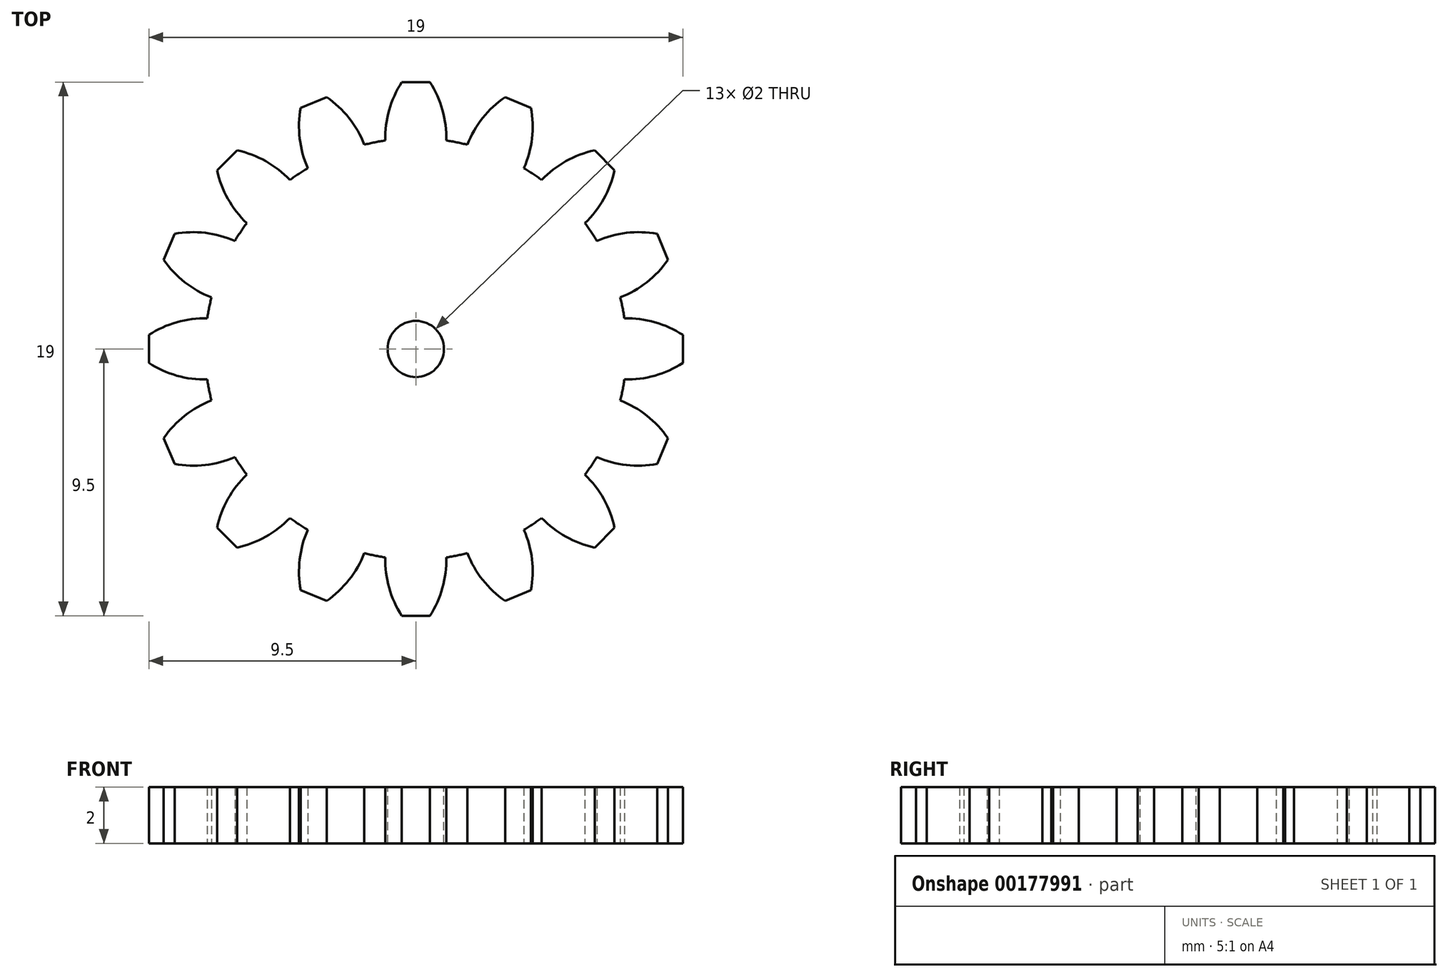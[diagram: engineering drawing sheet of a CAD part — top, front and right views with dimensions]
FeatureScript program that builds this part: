
annotation { "Feature Type Name" : "Feature", "Feature Type Description" : "" }
export const myFeature = defineFeature(function(context is Context, id is Id, definition is map)
    precondition{}
    {
        {
            var Q0;
            Q0=qCreatedBy(makeId("Top.planeOp"),FACE);
            var sketch = newSketch(context, id + "F0", { "sketchPlane" : qUnion([Q0])});
            skCircle(sketch, "E0", {"center": v(0, 0) * mm, "radius": 7.5 * mm});
            skLineSegment(sketch, "E1", {"start": v(0, 0) * mm, "end": v(0, 7.5) * mm, "construction": true});
            skLineSegment(sketch, "E2", {"start": v(0, 7.5) * mm, "end": v(0, 9.5) * mm, "construction": true});
            skLineSegment(sketch, "E3", {"start": v(0, 9.5) * mm, "end": v(-0.5, 9.5) * mm});
            skArc(sketch, "E4", {"start": v(-0.5, 9.5) * mm, "mid": v(-0.95, 8.5) * mm, "end": v(-1.09, 7.42) * mm});
            skLineSegment(sketch, "E5.MirrorCS", {"start": v(0, 9.5) * mm, "end": v(0.5, 9.5) * mm});
            skArc(sketch, "E6.MirrorCS", {"start": v(0.5, 9.5) * mm, "mid": v(0.95, 8.5) * mm, "end": v(1.09, 7.42) * mm});
            skArc(sketch, "E7.1.0", {"start": v(-4.1, 8.59) * mm, "mid": v(-4.13, 7.5) * mm, "end": v(-3.85, 6.44) * mm});
            skLineSegment(sketch, "E7.1.1", {"start": v(-3.64, 8.78) * mm, "end": v(-4.1, 8.59) * mm});
            skLineSegment(sketch, "E7.1.2", {"start": v(-3.64, 8.78) * mm, "end": v(-3.17, 8.97) * mm});
            skArc(sketch, "E7.1.3", {"start": v(-3.17, 8.97) * mm, "mid": v(-2.38, 8.22) * mm, "end": v(-1.83, 7.27) * mm});
            skArc(sketch, "E7.2.0", {"start": v(-7.07, 6.36) * mm, "mid": v(-6.69, 5.34) * mm, "end": v(-6.02, 4.48) * mm});
            skLineSegment(sketch, "E7.2.1", {"start": v(-6.72, 6.72) * mm, "end": v(-7.07, 6.36) * mm});
            skLineSegment(sketch, "E7.2.2", {"start": v(-6.72, 6.72) * mm, "end": v(-6.36, 7.07) * mm});
            skArc(sketch, "E7.2.3", {"start": v(-6.36, 7.07) * mm, "mid": v(-5.34, 6.69) * mm, "end": v(-4.48, 6.02) * mm});
            skArc(sketch, "E7.3.0", {"start": v(-8.97, 3.17) * mm, "mid": v(-8.22, 2.38) * mm, "end": v(-7.27, 1.83) * mm});
            skLineSegment(sketch, "E7.3.1", {"start": v(-8.78, 3.64) * mm, "end": v(-8.97, 3.17) * mm});
            skLineSegment(sketch, "E7.3.2", {"start": v(-8.78, 3.64) * mm, "end": v(-8.59, 4.1) * mm});
            skArc(sketch, "E7.3.3", {"start": v(-8.59, 4.1) * mm, "mid": v(-7.5, 4.13) * mm, "end": v(-6.44, 3.85) * mm});
            skArc(sketch, "E7.4.0", {"start": v(-9.5, -0.5) * mm, "mid": v(-8.5, -0.95) * mm, "end": v(-7.42, -1.09) * mm});
            skLineSegment(sketch, "E7.4.1", {"start": v(-9.5, 0) * mm, "end": v(-9.5, -0.5) * mm});
            skLineSegment(sketch, "E7.4.2", {"start": v(-9.5, 0) * mm, "end": v(-9.5, 0.5) * mm});
            skArc(sketch, "E7.4.3", {"start": v(-9.5, 0.5) * mm, "mid": v(-8.5, 0.95) * mm, "end": v(-7.42, 1.09) * mm});
            skArc(sketch, "E7.5.0", {"start": v(-8.59, -4.1) * mm, "mid": v(-7.5, -4.13) * mm, "end": v(-6.44, -3.85) * mm});
            skLineSegment(sketch, "E7.5.1", {"start": v(-8.78, -3.64) * mm, "end": v(-8.59, -4.1) * mm});
            skLineSegment(sketch, "E7.5.2", {"start": v(-8.78, -3.64) * mm, "end": v(-8.97, -3.17) * mm});
            skArc(sketch, "E7.5.3", {"start": v(-8.97, -3.17) * mm, "mid": v(-8.22, -2.38) * mm, "end": v(-7.27, -1.83) * mm});
            skArc(sketch, "E7.6.0", {"start": v(-6.36, -7.07) * mm, "mid": v(-5.34, -6.69) * mm, "end": v(-4.48, -6.02) * mm});
            skLineSegment(sketch, "E7.6.1", {"start": v(-6.72, -6.72) * mm, "end": v(-6.36, -7.07) * mm});
            skLineSegment(sketch, "E7.6.2", {"start": v(-6.72, -6.72) * mm, "end": v(-7.07, -6.36) * mm});
            skArc(sketch, "E7.6.3", {"start": v(-7.07, -6.36) * mm, "mid": v(-6.69, -5.34) * mm, "end": v(-6.02, -4.48) * mm});
            skArc(sketch, "E7.7.0", {"start": v(-3.17, -8.97) * mm, "mid": v(-2.38, -8.22) * mm, "end": v(-1.83, -7.27) * mm});
            skLineSegment(sketch, "E7.7.1", {"start": v(-3.64, -8.78) * mm, "end": v(-3.17, -8.97) * mm});
            skLineSegment(sketch, "E7.7.2", {"start": v(-3.64, -8.78) * mm, "end": v(-4.1, -8.59) * mm});
            skArc(sketch, "E7.7.3", {"start": v(-4.1, -8.59) * mm, "mid": v(-4.13, -7.5) * mm, "end": v(-3.85, -6.44) * mm});
            skArc(sketch, "E7.8.0", {"start": v(0.5, -9.5) * mm, "mid": v(0.95, -8.5) * mm, "end": v(1.09, -7.42) * mm});
            skLineSegment(sketch, "E7.8.1", {"start": v(0, -9.5) * mm, "end": v(0.5, -9.5) * mm});
            skLineSegment(sketch, "E7.8.2", {"start": v(0, -9.5) * mm, "end": v(-0.5, -9.5) * mm});
            skArc(sketch, "E7.8.3", {"start": v(-0.5, -9.5) * mm, "mid": v(-0.95, -8.5) * mm, "end": v(-1.09, -7.42) * mm});
            skArc(sketch, "E7.9.0", {"start": v(4.1, -8.59) * mm, "mid": v(4.13, -7.5) * mm, "end": v(3.85, -6.44) * mm});
            skLineSegment(sketch, "E7.9.1", {"start": v(3.64, -8.78) * mm, "end": v(4.1, -8.59) * mm});
            skLineSegment(sketch, "E7.9.2", {"start": v(3.64, -8.78) * mm, "end": v(3.17, -8.97) * mm});
            skArc(sketch, "E7.9.3", {"start": v(3.17, -8.97) * mm, "mid": v(2.38, -8.22) * mm, "end": v(1.83, -7.27) * mm});
            skArc(sketch, "E7.10.0", {"start": v(7.07, -6.36) * mm, "mid": v(6.69, -5.34) * mm, "end": v(6.02, -4.48) * mm});
            skLineSegment(sketch, "E7.10.1", {"start": v(6.72, -6.72) * mm, "end": v(7.07, -6.36) * mm});
            skLineSegment(sketch, "E7.10.2", {"start": v(6.72, -6.72) * mm, "end": v(6.36, -7.07) * mm});
            skArc(sketch, "E7.10.3", {"start": v(6.36, -7.07) * mm, "mid": v(5.34, -6.69) * mm, "end": v(4.48, -6.02) * mm});
            skArc(sketch, "E7.11.0", {"start": v(8.97, -3.17) * mm, "mid": v(8.22, -2.38) * mm, "end": v(7.27, -1.83) * mm});
            skLineSegment(sketch, "E7.11.1", {"start": v(8.78, -3.64) * mm, "end": v(8.97, -3.17) * mm});
            skLineSegment(sketch, "E7.11.2", {"start": v(8.78, -3.64) * mm, "end": v(8.59, -4.1) * mm});
            skArc(sketch, "E7.11.3", {"start": v(8.59, -4.1) * mm, "mid": v(7.5, -4.13) * mm, "end": v(6.44, -3.85) * mm});
            skArc(sketch, "E7.12.0", {"start": v(9.5, 0.5) * mm, "mid": v(8.5, 0.95) * mm, "end": v(7.42, 1.09) * mm});
            skLineSegment(sketch, "E7.12.1", {"start": v(9.5, 0) * mm, "end": v(9.5, 0.5) * mm});
            skLineSegment(sketch, "E7.12.2", {"start": v(9.5, 0) * mm, "end": v(9.5, -0.5) * mm});
            skArc(sketch, "E7.12.3", {"start": v(9.5, -0.5) * mm, "mid": v(8.5, -0.95) * mm, "end": v(7.42, -1.09) * mm});
            skArc(sketch, "E7.13.0", {"start": v(8.59, 4.1) * mm, "mid": v(7.5, 4.13) * mm, "end": v(6.44, 3.85) * mm});
            skLineSegment(sketch, "E7.13.1", {"start": v(8.78, 3.64) * mm, "end": v(8.59, 4.1) * mm});
            skLineSegment(sketch, "E7.13.2", {"start": v(8.78, 3.64) * mm, "end": v(8.97, 3.17) * mm});
            skArc(sketch, "E7.13.3", {"start": v(8.97, 3.17) * mm, "mid": v(8.22, 2.38) * mm, "end": v(7.27, 1.83) * mm});
            skArc(sketch, "E7.14.0", {"start": v(6.36, 7.07) * mm, "mid": v(5.34, 6.69) * mm, "end": v(4.48, 6.02) * mm});
            skLineSegment(sketch, "E7.14.1", {"start": v(6.72, 6.72) * mm, "end": v(6.36, 7.07) * mm});
            skLineSegment(sketch, "E7.14.2", {"start": v(6.72, 6.72) * mm, "end": v(7.07, 6.36) * mm});
            skArc(sketch, "E7.14.3", {"start": v(7.07, 6.36) * mm, "mid": v(6.69, 5.34) * mm, "end": v(6.02, 4.48) * mm});
            skArc(sketch, "E7.15.0", {"start": v(3.17, 8.97) * mm, "mid": v(2.38, 8.22) * mm, "end": v(1.83, 7.27) * mm});
            skLineSegment(sketch, "E7.15.1", {"start": v(3.64, 8.78) * mm, "end": v(3.17, 8.97) * mm});
            skLineSegment(sketch, "E7.15.2", {"start": v(3.64, 8.78) * mm, "end": v(4.1, 8.59) * mm});
            skArc(sketch, "E7.15.3", {"start": v(4.1, 8.59) * mm, "mid": v(4.13, 7.5) * mm, "end": v(3.85, 6.44) * mm});
            skSolve(sketch);
        }
        {
            var Q0;
            Q0 = qSketchRegion(id + "F0", true);
            extrude(context, id + "F1", {"entities" : qUnion([Q0]), "depth" : 2 * mm});
        }
        {
            var Q0;
            Q0=makeQuery(id+"F1.opExtrude","CAP_FACE",FACE,{"disambiguationData":[OSD([sQuery(id+"F0.wireOp",EDGE,"E0"),sQuery(id+"F0.wireOp",EDGE,"E3"),sQuery(id+"F0.wireOp",EDGE,"E4"),sQuery(id+"F0.wireOp",EDGE,"E5.MirrorCS"),sQuery(id+"F0.wireOp",EDGE,"E6.MirrorCS"),sQuery(id+"F0.wireOp",EDGE,"E7.1.0"),sQuery(id+"F0.wireOp",EDGE,"E7.1.1"),sQuery(id+"F0.wireOp",EDGE,"E7.1.2"),sQuery(id+"F0.wireOp",EDGE,"E7.1.3"),sQuery(id+"F0.wireOp",EDGE,"E7.2.0"),sQuery(id+"F0.wireOp",EDGE,"E7.2.1"),sQuery(id+"F0.wireOp",EDGE,"E7.2.2"),sQuery(id+"F0.wireOp",EDGE,"E7.2.3"),sQuery(id+"F0.wireOp",EDGE,"E7.3.0"),sQuery(id+"F0.wireOp",EDGE,"E7.3.1"),sQuery(id+"F0.wireOp",EDGE,"E7.3.2"),sQuery(id+"F0.wireOp",EDGE,"E7.3.3"),sQuery(id+"F0.wireOp",EDGE,"E7.4.0"),sQuery(id+"F0.wireOp",EDGE,"E7.4.1"),sQuery(id+"F0.wireOp",EDGE,"E7.4.2"),sQuery(id+"F0.wireOp",EDGE,"E7.4.3"),sQuery(id+"F0.wireOp",EDGE,"E7.5.0"),sQuery(id+"F0.wireOp",EDGE,"E7.5.1"),sQuery(id+"F0.wireOp",EDGE,"E7.5.2"),sQuery(id+"F0.wireOp",EDGE,"E7.5.3"),sQuery(id+"F0.wireOp",EDGE,"E7.6.0"),sQuery(id+"F0.wireOp",EDGE,"E7.6.1"),sQuery(id+"F0.wireOp",EDGE,"E7.6.2"),sQuery(id+"F0.wireOp",EDGE,"E7.6.3"),sQuery(id+"F0.wireOp",EDGE,"E7.7.0"),sQuery(id+"F0.wireOp",EDGE,"E7.7.1"),sQuery(id+"F0.wireOp",EDGE,"E7.7.2"),sQuery(id+"F0.wireOp",EDGE,"E7.7.3"),sQuery(id+"F0.wireOp",EDGE,"E7.8.0"),sQuery(id+"F0.wireOp",EDGE,"E7.8.1"),sQuery(id+"F0.wireOp",EDGE,"E7.8.2"),sQuery(id+"F0.wireOp",EDGE,"E7.8.3"),sQuery(id+"F0.wireOp",EDGE,"E7.9.0"),sQuery(id+"F0.wireOp",EDGE,"E7.9.1"),sQuery(id+"F0.wireOp",EDGE,"E7.9.2"),sQuery(id+"F0.wireOp",EDGE,"E7.9.3"),sQuery(id+"F0.wireOp",EDGE,"E7.10.0"),sQuery(id+"F0.wireOp",EDGE,"E7.10.1"),sQuery(id+"F0.wireOp",EDGE,"E7.10.2"),sQuery(id+"F0.wireOp",EDGE,"E7.10.3"),sQuery(id+"F0.wireOp",EDGE,"E7.11.0"),sQuery(id+"F0.wireOp",EDGE,"E7.11.1"),sQuery(id+"F0.wireOp",EDGE,"E7.11.2"),sQuery(id+"F0.wireOp",EDGE,"E7.11.3"),sQuery(id+"F0.wireOp",EDGE,"E7.12.0"),sQuery(id+"F0.wireOp",EDGE,"E7.12.1"),sQuery(id+"F0.wireOp",EDGE,"E7.12.2"),sQuery(id+"F0.wireOp",EDGE,"E7.12.3"),sQuery(id+"F0.wireOp",EDGE,"E7.13.0"),sQuery(id+"F0.wireOp",EDGE,"E7.13.1"),sQuery(id+"F0.wireOp",EDGE,"E7.13.2"),sQuery(id+"F0.wireOp",EDGE,"E7.13.3"),sQuery(id+"F0.wireOp",EDGE,"E7.14.0"),sQuery(id+"F0.wireOp",EDGE,"E7.14.1"),sQuery(id+"F0.wireOp",EDGE,"E7.14.2"),sQuery(id+"F0.wireOp",EDGE,"E7.14.3"),sQuery(id+"F0.wireOp",EDGE,"E7.15.0"),sQuery(id+"F0.wireOp",EDGE,"E7.15.1"),sQuery(id+"F0.wireOp",EDGE,"E7.15.2"),sQuery(id+"F0.wireOp",EDGE,"E7.15.3")])],"isStart":false});
            var sketch = newSketch(context, id + "F2", { "sketchPlane" : qUnion([Q0])});
            skCircle(sketch, "E8", {"center": v(0, 0) * mm, "radius": 1 * mm});
            skSolve(sketch);
        }
        {
            var Q0;
            Q0 = qSketchRegion(id + "F2", true);
            extrude(context, id + "F3", {"entities" : qUnion([Q0]), "operationType" : NewBodyOperationType.REMOVE, "endBound" : BoundingType.THROUGH_ALL, "oppositeDirection" : true, "depth" : 25 * mm});
        }
    });
